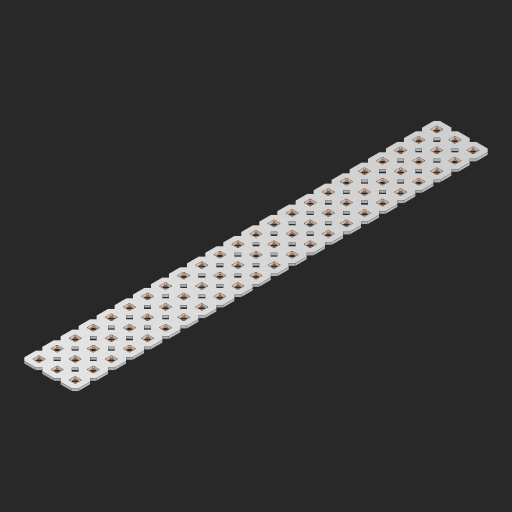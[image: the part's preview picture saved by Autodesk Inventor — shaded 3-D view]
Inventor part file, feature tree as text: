
AUTODESK INVENTOR PART (.ipt)
format: ipt  version: 2023 (Build 270158000, 158)  size: 1,072,640 bytes
history: native  units: in
note: dims shown in document units (in); Inventor stores cm internally (conversion verified against a paired STEP export)
features: other x70, extrude x68, sketch x2, pattern_linear x1
ambient origin geometry x8: Origin, YZ Plane, XZ Plane, XY Plane, X Axis, Y Axis, Z Axis, Center Point
bodies: Solid1 (feature_tree), Body (feature_tree)
feature tree (141):
  pattern_linear  "Rectangular Pattern1"  Spacing1=0.09in  [1 undecoded]
  sketch  "Sketch1"  dims[d1=0.5in]
  sketch  "Sketch2"  dims[d2=0.182in d3=0.09in d4=0.09in d5=0.09in d6=0.09in d7=0.09in d8=0.09in d9=0.09in d10=0.09in d11=0.02in d13=0.0in d14=0.172in d15=0.0625in d16=0.0in d19=0.5in d22=0.5in]
  other  "Srf1"
  other  "Srf126"
  other  "Srf127"
  other  "Srf128"
  other  "Srf129"
  other  "Srf130"
  other  "Srf131"
  other  "Srf250"
  other  "Srf251"
  other  "Srf252"
  other  "Srf253"
  other  "Srf254"
  other  "Srf255"
  other  "Srf256"
  other  "Srf257"
  other  "Srf258"
  other  "Srf259"
  other  "Srf260"
  other  "Srf261"
  other  "Srf262"
  other  "Srf263"
  other  "Srf264"
  other  "Srf265"
  other  "Srf268"
  other  "Srf269"
  other  "Srf270"
  other  "Srf271"
  other  "Srf272"
  other  "Srf273"
  other  "Srf274"
  other  "Srf275"
  other  "Srf276"
  other  "Srf277"
  other  "Srf278"
  other  "Srf279"
  other  "Srf280"
  other  "Srf281"
  other  "Srf282"
  other  "Srf283"
  other  "Srf284"
  other  "Srf285"
  other  "Srf286"
  other  "Srf287"
  other  "Srf288"
  other  "Srf289"
  other  "Srf290"
  other  "Srf293"
  other  "Srf294"
  other  "Srf295"
  other  "Srf296"
  other  "Srf297"
  other  "Srf298"
  other  "Srf299"
  other  "Srf300"
  other  "Srf301"
  other  "Srf302"
  other  "Srf303"
  other  "Srf304"
  other  "Srf305"
  other  "Srf306"
  other  "Srf307"
  other  "Srf308"
  other  "Srf309"
  other  "Srf310"
  other  "Srf311"
  other  "Srf312"
  other  "Srf313"
  other  "Srf314"
  other  "Srf315"
  other  "Circle"
  extrude  "ExtrusionSrf126"  Depth=0.09in
  extrude  "ExtrusionSrf127"  Depth=0.09in
  extrude  "ExtrusionSrf128"  Depth=0.09in
  extrude  "ExtrusionSrf129"  Depth=0.09in
  extrude  "ExtrusionSrf130"  Depth=0.09in
  extrude  "ExtrusionSrf131"  Depth=0.09in
  extrude  "ExtrusionSrf250"  Depth=0.09in
  extrude  "ExtrusionSrf251"  Depth=0.02in
  extrude  "ExtrusionSrf252"  TaperAngle=0.0deg  [1 undecoded]
  extrude  "ExtrusionSrf253"  Depth=0.5in
  extrude  "ExtrusionSrf254"  Depth=0.0625in TaperAngle=0.0deg
  extrude  "ExtrusionSrf255"  Depth=0.5in
  extrude  "ExtrusionSrf256"  Depth=0.5in
  extrude  "ExtrusionSrf257"  [1 undecoded]
  extrude  "ExtrusionSrf258"  [1 undecoded]
  extrude  "ExtrusionSrf259"  [1 undecoded]
  extrude  "ExtrusionSrf260"  [1 undecoded]
  extrude  "ExtrusionSrf261"  [1 undecoded]
  extrude  "ExtrusionSrf262"  [1 undecoded]
  extrude  "ExtrusionSrf263"  [1 undecoded]
  extrude  "ExtrusionSrf264"  [1 undecoded]
  extrude  "ExtrusionSrf265"  [1 undecoded]
  extrude  "ExtrusionSrf268"  [1 undecoded]
  extrude  "ExtrusionSrf269"  [1 undecoded]
  extrude  "ExtrusionSrf270"  [1 undecoded]
  extrude  "ExtrusionSrf271"  [1 undecoded]
  extrude  "ExtrusionSrf272"  [1 undecoded]
  extrude  "ExtrusionSrf273"  [1 undecoded]
  extrude  "ExtrusionSrf274"  [1 undecoded]
  extrude  "ExtrusionSrf275"  [1 undecoded]
  extrude  "ExtrusionSrf276"  [1 undecoded]
  extrude  "ExtrusionSrf277"  [1 undecoded]
  extrude  "ExtrusionSrf278"  [1 undecoded]
  extrude  "ExtrusionSrf279"  [1 undecoded]
  extrude  "ExtrusionSrf280"  [1 undecoded]
  extrude  "ExtrusionSrf281"  [1 undecoded]
  extrude  "ExtrusionSrf282"  [1 undecoded]
  extrude  "ExtrusionSrf283"  [1 undecoded]
  extrude  "ExtrusionSrf284"  [1 undecoded]
  extrude  "ExtrusionSrf285"  [1 undecoded]
  extrude  "ExtrusionSrf286"  [1 undecoded]
  extrude  "ExtrusionSrf287"  [1 undecoded]
  extrude  "ExtrusionSrf288"  [1 undecoded]
  extrude  "ExtrusionSrf289"  [1 undecoded]
  extrude  "ExtrusionSrf290"  [1 undecoded]
  extrude  "ExtrusionSrf293"  [1 undecoded]
  extrude  "ExtrusionSrf294"  [1 undecoded]
  extrude  "ExtrusionSrf295"  [1 undecoded]
  extrude  "ExtrusionSrf296"  [1 undecoded]
  extrude  "ExtrusionSrf297"  [1 undecoded]
  extrude  "ExtrusionSrf298"  [1 undecoded]
  extrude  "ExtrusionSrf299"  [1 undecoded]
  extrude  "ExtrusionSrf300"  [1 undecoded]
  extrude  "ExtrusionSrf301"  [1 undecoded]
  extrude  "ExtrusionSrf302"  [1 undecoded]
  extrude  "ExtrusionSrf303"  [1 undecoded]
  extrude  "ExtrusionSrf304"  [1 undecoded]
  extrude  "ExtrusionSrf305"  [1 undecoded]
  extrude  "ExtrusionSrf306"  [1 undecoded]
  extrude  "ExtrusionSrf307"  [1 undecoded]
  extrude  "ExtrusionSrf308"  [1 undecoded]
  extrude  "ExtrusionSrf309"  [1 undecoded]
  extrude  "ExtrusionSrf310"  [1 undecoded]
  extrude  "ExtrusionSrf311"  [1 undecoded]
  extrude  "ExtrusionSrf312"  [1 undecoded]
  extrude  "ExtrusionSrf313"  [1 undecoded]
  extrude  "ExtrusionSrf314"  [1 undecoded]
  extrude  "ExtrusionSrf315"  [1 undecoded]
note: 57 required parameter values undecoded (feature->parameter linkage not recoverable at this tier; creation-order binding heuristic only, values carry confidence <= 0.55)
